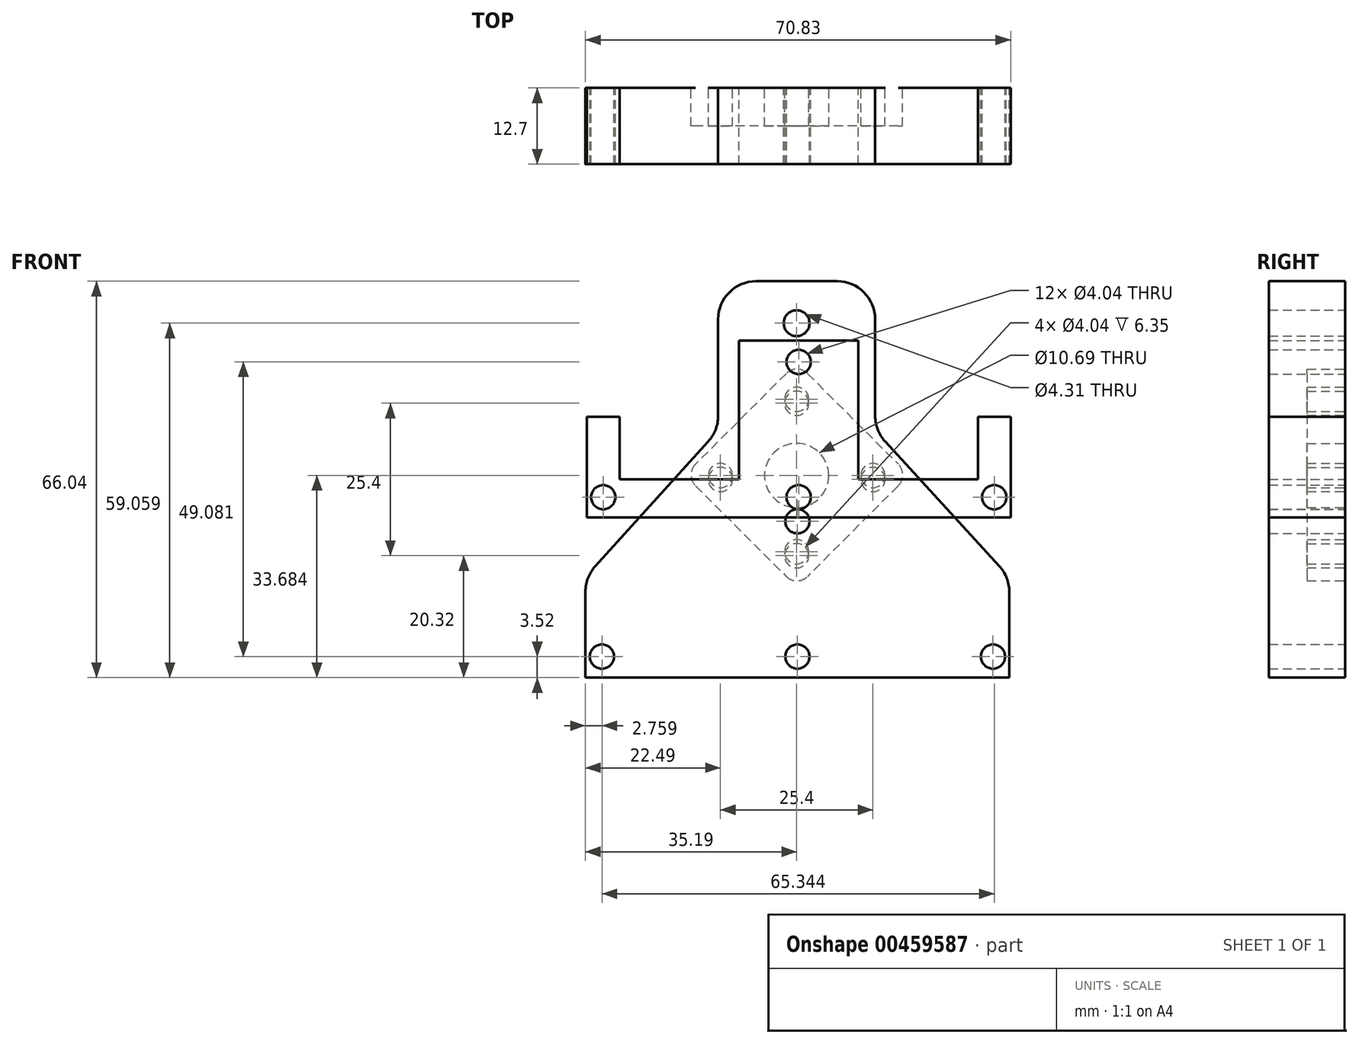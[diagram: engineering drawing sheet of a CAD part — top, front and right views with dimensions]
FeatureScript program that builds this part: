
annotation { "Feature Type Name" : "Feature", "Feature Type Description" : "" }
export const myFeature = defineFeature(function(context is Context, id is Id, definition is map)
    precondition{}
    {
        {
            var Q0;
            Q0=qCreatedBy(makeId("Front.planeOp"),FACE);
            var sketch = newSketch(context, id + "F0", { "sketchPlane" : qUnion([Q0])});
            skLineSegment(sketch, "E0.top", {"start": v(-35.19, -33.02) * mm, "end": v(34.92, -33.02) * mm});
            skLineSegment(sketch, "E1", {"start": v(35.43, -32.5) * mm, "end": v(35.43, -18.72) * mm});
            skLineSegment(sketch, "E2", {"start": v(-35.19, -33.02) * mm, "end": v(-35.19, -18.7) * mm});
            skLineSegment(sketch, "E3", {"start": v(-6.73, 33.02) * mm, "end": v(6.73, 33.02) * mm});
            skLineSegment(sketch, "E4", {"start": v(-13.08, 26.67) * mm, "end": v(-13.08, 10.58) * mm});
            skLineSegment(sketch, "E5", {"start": v(13.08, 26.67) * mm, "end": v(13.08, 10.6) * mm});
            skLineSegment(sketch, "E6", {"start": v(-14.73, 6.31) * mm, "end": v(-33.54, -14.44) * mm});
            skLineSegment(sketch, "E7", {"start": v(14.75, 6.3) * mm, "end": v(33.76, -14.43) * mm});
            skPoint(sketch, "E8.visualSharp", {"position": v(-13.08, 8.13) * mm});
            skArc(sketch, "E8.filletArc", {"start": v(-14.73, 6.31) * mm, "mid": v(-13.5, 8.3) * mm, "end": v(-13.08, 10.58) * mm});
            skPoint(sketch, "E9.visualSharp", {"position": v(13.08, 8.13) * mm});
            skArc(sketch, "E9.filletArc", {"start": v(13.08, 10.6) * mm, "mid": v(13.51, 8.3) * mm, "end": v(14.75, 6.3) * mm});
            skPoint(sketch, "E10.visualSharp", {"position": v(-13.08, 33.02) * mm});
            skArc(sketch, "E10.filletArc", {"start": v(-6.73, 33.02) * mm, "mid": v(-11.22, 31.16) * mm, "end": v(-13.08, 26.67) * mm});
            skPoint(sketch, "E11.visualSharp", {"position": v(13.08, 33.02) * mm});
            skArc(sketch, "E11.filletArc", {"start": v(13.08, 26.67) * mm, "mid": v(11.22, 31.16) * mm, "end": v(6.73, 33.02) * mm});
            skPoint(sketch, "E12.visualSharp", {"position": v(-35.19, -16.25) * mm});
            skArc(sketch, "E12.filletArc", {"start": v(-33.54, -14.44) * mm, "mid": v(-34.76, -16.42) * mm, "end": v(-35.19, -18.7) * mm});
            skPoint(sketch, "E13.visualSharp", {"position": v(35.43, -16.25) * mm});
            skArc(sketch, "E13.filletArc", {"start": v(35.43, -18.72) * mm, "mid": v(35, -16.42) * mm, "end": v(33.76, -14.43) * mm});
            skPoint(sketch, "E14.visualSharp", {"position": v(35.43, -33.02) * mm});
            skPoint(sketch, "E15.endSnap0", {"position": v(0, 33.02) * mm});
            skLineSegment(sketch, "E16", {"start": v(35.43, -32.5) * mm, "end": v(35.43, -33.02) * mm});
            skLineSegment(sketch, "E17", {"start": v(35.43, -33.02) * mm, "end": v(34.92, -33.02) * mm});
            skCircle(sketch, "E18", {"center": v(0.12, -6.97) * mm, "radius": 2.02 * mm});
            skCircle(sketch, "E19", {"center": v(32.7, -29.5) * mm, "radius": 2.02 * mm});
            skCircle(sketch, "E20", {"center": v(0.12, -29.5) * mm, "radius": 2.02 * mm});
            skCircle(sketch, "E21", {"center": v(-32.43, -29.5) * mm, "radius": 2.02 * mm});
            skLineSegment(sketch, "E22", {"start": v(-12, 19.69) * mm, "end": v(11.92, 19.69) * mm});
            skCircle(sketch, "E23", {"center": v(0, 26.04) * mm, "radius": 2.15 * mm});
            skSolve(sketch);
        }
        {
            var Q0;
            Q0=makeQuery(id+"F0.imprint","IMPRINT",FACE,{"disambiguationData":[TD([[makeQuery(id+"F0.imprint","IMPRINT",EDGE,{"derivedFrom":sQuery(id+"F0.wireOp",EDGE,"E0.top")}),1.0]])]});
            extrude(context, id + "F1", {"entities" : qUnion([Q0]), "depth" : 12.7 * mm});
        }
        {
            var Q0;
            Q0=makeQuery(id+"F1.opExtrude","CAP_FACE",FACE,{"disambiguationData":[OSD([sQuery(id+"F0.wireOp",EDGE,"E0.top"),sQuery(id+"F0.wireOp",EDGE,"E1"),sQuery(id+"F0.wireOp",EDGE,"E2"),sQuery(id+"F0.wireOp",EDGE,"E3"),sQuery(id+"F0.wireOp",EDGE,"E4"),sQuery(id+"F0.wireOp",EDGE,"E5"),sQuery(id+"F0.wireOp",EDGE,"E6"),sQuery(id+"F0.wireOp",EDGE,"E7"),sQuery(id+"F0.wireOp",EDGE,"E8.filletArc"),sQuery(id+"F0.wireOp",EDGE,"E9.filletArc"),sQuery(id+"F0.wireOp",EDGE,"E10.filletArc"),sQuery(id+"F0.wireOp",EDGE,"E11.filletArc"),sQuery(id+"F0.wireOp",EDGE,"E12.filletArc"),sQuery(id+"F0.wireOp",EDGE,"E13.filletArc"),sQuery(id+"F0.wireOp",EDGE,"E14.filletArc")])],"isStart":true});
            var sketch = newSketch(context, id + "F2", { "sketchPlane" : qUnion([Q0])});
            skCircle(sketch, "E24", {"center": v(0, 12.7) * mm, "radius": 2.02 * mm});
            skCircle(sketch, "E25", {"center": v(12.7, 0) * mm, "radius": 2.02 * mm});
            skCircle(sketch, "E26", {"center": v(0, -12.7) * mm, "radius": 2.02 * mm});
            skCircle(sketch, "E27", {"center": v(-12.7, 0) * mm, "radius": 2.02 * mm});
            skSolve(sketch);
        }
        {
            var Q0;
            Q0=makeQuery(id+"F2.imprint","IMPRINT",FACE,{"disambiguationData":[TD([[makeQuery(id+"F2.imprint","IMPRINT",EDGE,{"derivedFrom":sQuery(id+"F2.wireOp",EDGE,"E24")}),1.0]])]});
            var Q1;
            Q1=makeQuery(id+"F2.imprint","IMPRINT",FACE,{"disambiguationData":[TD([[makeQuery(id+"F2.imprint","IMPRINT",EDGE,{"derivedFrom":sQuery(id+"F2.wireOp",EDGE,"E27")}),1.0]])]});
            var Q2;
            Q2=makeQuery(id+"F2.imprint","IMPRINT",FACE,{"disambiguationData":[TD([[makeQuery(id+"F2.imprint","IMPRINT",EDGE,{"derivedFrom":sQuery(id+"F2.wireOp",EDGE,"E25")}),1.0]])]});
            var Q3;
            Q3=makeQuery(id+"F2.imprint","IMPRINT",FACE,{"disambiguationData":[TD([[makeQuery(id+"F2.imprint","IMPRINT",EDGE,{"derivedFrom":sQuery(id+"F2.wireOp",EDGE,"E26")}),1.0]])]});
            extrude(context, id + "F3", {"entities" : qUnion([Q0, Q1, Q2, Q3]), "operationType" : NewBodyOperationType.REMOVE, "oppositeDirection" : true, "depth" : 6.35 * mm});
        }
        {
            var Q0;
            Q0=makeQuery(id+"F1.opExtrude","CAP_FACE",FACE,{"disambiguationData":[OSD([sQuery(id+"F0.wireOp",EDGE,"E0.top"),sQuery(id+"F0.wireOp",EDGE,"E1"),sQuery(id+"F0.wireOp",EDGE,"E2"),sQuery(id+"F0.wireOp",EDGE,"E3"),sQuery(id+"F0.wireOp",EDGE,"E4"),sQuery(id+"F0.wireOp",EDGE,"E5"),sQuery(id+"F0.wireOp",EDGE,"E6"),sQuery(id+"F0.wireOp",EDGE,"E7"),sQuery(id+"F0.wireOp",EDGE,"E8.filletArc"),sQuery(id+"F0.wireOp",EDGE,"E9.filletArc"),sQuery(id+"F0.wireOp",EDGE,"E10.filletArc"),sQuery(id+"F0.wireOp",EDGE,"E11.filletArc"),sQuery(id+"F0.wireOp",EDGE,"E12.filletArc"),sQuery(id+"F0.wireOp",EDGE,"E13.filletArc"),sQuery(id+"F0.wireOp",EDGE,"E14.filletArc")])],"isStart":true});
            var sketch = newSketch(context, id + "F4", { "sketchPlane" : qUnion([Q0])});
            skLineSegment(sketch, "E28.bottom", {"start": v(-1.8, 16.88) * mm, "end": v(-16.88, 1.8) * mm});
            skLineSegment(sketch, "E28.top", {"start": v(16.88, -1.8) * mm, "end": v(1.8, -16.88) * mm});
            skLineSegment(sketch, "E28.left", {"start": v(1.8, 16.88) * mm, "end": v(16.88, 1.8) * mm});
            skLineSegment(sketch, "E28.right", {"start": v(-16.88, -1.8) * mm, "end": v(-1.8, -16.88) * mm});
            skPoint(sketch, "E28.middle", {"position": v(0, 0) * mm});
            skPoint(sketch, "E29.visualSharp", {"position": v(0, 18.68) * mm});
            skArc(sketch, "E29.filletArc", {"start": v(1.8, 16.88) * mm, "mid": v(0, 17.63) * mm, "end": v(-1.8, 16.88) * mm});
            skPoint(sketch, "E30.visualSharp", {"position": v(-18.68, 0) * mm});
            skArc(sketch, "E30.filletArc", {"start": v(-16.88, 1.8) * mm, "mid": v(-17.63, 0) * mm, "end": v(-16.88, -1.8) * mm});
            skPoint(sketch, "E31.visualSharp", {"position": v(0, -18.68) * mm});
            skArc(sketch, "E31.filletArc", {"start": v(-1.8, -16.88) * mm, "mid": v(0, -17.63) * mm, "end": v(1.8, -16.88) * mm});
            skPoint(sketch, "E32.visualSharp", {"position": v(18.68, 0) * mm});
            skArc(sketch, "E32.filletArc", {"start": v(16.88, -1.8) * mm, "mid": v(17.63, 0) * mm, "end": v(16.88, 1.8) * mm});
            skSolve(sketch);
        }
        {
            var Q0;
            Q0=makeQuery(id+"F4.imprint","IMPRINT",FACE,{"disambiguationData":[TD([[makeQuery(id+"F4.imprint","IMPRINT",EDGE,{"derivedFrom":sQuery(id+"F4.wireOp",EDGE,"E28.bottom")}),1.0]])]});
            extrude(context, id + "F5", {"entities" : qUnion([Q0]), "depth" : 6.35 * mm});
        }
        {
            var Q0;
            Q0=qCreatedBy(makeId("Front.planeOp"),FACE);
            var sketch = newSketch(context, id + "F6", { "sketchPlane" : qUnion([Q0])});
            skLineSegment(sketch, "E33", {"start": v(35.64, -6.35) * mm, "end": v(-34.97, -6.35) * mm});
            skLineSegment(sketch, "E34", {"start": v(35.64, -6.35) * mm, "end": v(35.64, 10.41) * mm});
            skLineSegment(sketch, "E35", {"start": v(-34.97, -6.35) * mm, "end": v(-34.97, 10.41) * mm});
            skLineSegment(sketch, "E36", {"start": v(35.64, 10.41) * mm, "end": v(30.18, 10.41) * mm});
            skLineSegment(sketch, "E37", {"start": v(-34.97, 10.41) * mm, "end": v(-29.5, 10.41) * mm});
            skLineSegment(sketch, "E38", {"start": v(30.18, 0) * mm, "end": v(10.3, 0) * mm});
            skLineSegment(sketch, "E39", {"start": v(-9.62, 23.11) * mm, "end": v(10.3, 23.11) * mm});
            skLineSegment(sketch, "E40", {"start": v(30.18, 10.41) * mm, "end": v(30.18, 0) * mm});
            skLineSegment(sketch, "E41", {"start": v(10.3, 23.11) * mm, "end": v(10.3, 0) * mm});
            skLineSegment(sketch, "E42", {"start": v(-9.62, 23.11) * mm, "end": v(-9.62, 0) * mm});
            skLineSegment(sketch, "E43", {"start": v(-29.5, 10.41) * mm, "end": v(-29.5, 0) * mm});
            skLineSegment(sketch, "E44", {"start": v(-29.5, 0) * mm, "end": v(-9.62, 0) * mm});
            skCircle(sketch, "E45", {"center": v(0.34, 19.58) * mm, "radius": 2.02 * mm});
            skCircle(sketch, "E46", {"center": v(32.91, -2.95) * mm, "radius": 2.02 * mm});
            skCircle(sketch, "E47", {"center": v(0.34, -2.95) * mm, "radius": 2.02 * mm});
            skCircle(sketch, "E48", {"center": v(-32.22, -2.95) * mm, "radius": 2.02 * mm});
            skPoint(sketch, "E49", {"position": v(4.04, 9.76) * mm});
            skSolve(sketch);
        }
        {
            var Q0;
            Q0=makeQuery(id+"F6.imprint","IMPRINT",FACE,{"disambiguationData":[TD([[makeQuery(id+"F6.imprint","IMPRINT",EDGE,{"derivedFrom":sQuery(id+"F6.wireOp",EDGE,"E33")}),-1.0]])]});
            extrude(context, id + "F7", {"entities" : qUnion([Q0]), "depth" : 12.7 * mm});
        }
        {
            var Q0;
            Q0=qCreatedBy(makeId("Front.planeOp"),FACE);
            var sketch = newSketch(context, id + "F8", { "sketchPlane" : qUnion([Q0])});
            skCircle(sketch, "E50", {"center": v(0, 13.36) * mm, "radius": 2.02 * mm});
            skCircle(sketch, "E51", {"center": v(12.7, 0.66) * mm, "radius": 2.02 * mm});
            skCircle(sketch, "E52", {"center": v(0, -12.04) * mm, "radius": 2.02 * mm});
            skCircle(sketch, "E53", {"center": v(-12.7, 0.66) * mm, "radius": 2.02 * mm});
            skLineSegment(sketch, "E54.bottom", {"start": v(-1.76, 17.63) * mm, "end": v(-16.84, 2.54) * mm});
            skLineSegment(sketch, "E54.top", {"start": v(16.92, -1.05) * mm, "end": v(1.84, -16.14) * mm});
            skLineSegment(sketch, "E54.left", {"start": v(1.84, 17.63) * mm, "end": v(16.92, 2.54) * mm});
            skLineSegment(sketch, "E54.right", {"start": v(-16.84, -1.05) * mm, "end": v(-1.76, -16.14) * mm});
            skArc(sketch, "E55.filletArc", {"start": v(1.84, 17.63) * mm, "mid": v(0.04, 18.37) * mm, "end": v(-1.76, 17.63) * mm});
            skArc(sketch, "E56.filletArc", {"start": v(-16.84, 2.54) * mm, "mid": v(-17.59, 0.75) * mm, "end": v(-16.84, -1.05) * mm});
            skArc(sketch, "E57.filletArc", {"start": v(-1.76, -16.14) * mm, "mid": v(0.04, -16.88) * mm, "end": v(1.84, -16.14) * mm});
            skArc(sketch, "E58.filletArc", {"start": v(16.92, -1.05) * mm, "mid": v(17.67, 0.75) * mm, "end": v(16.92, 2.54) * mm});
            skCircle(sketch, "E59", {"center": v(0, 0.66) * mm, "radius": 5.35 * mm});
            skSolve(sketch);
        }
        {
            var Q0;
            Q0=makeQuery(id+"F8.imprint","IMPRINT",FACE,{"disambiguationData":[TD([[makeQuery(id+"F8.imprint","IMPRINT",EDGE,{"derivedFrom":sQuery(id+"F8.wireOp",EDGE,"E50")}),-1.0]])]});
            extrude(context, id + "F9", {"entities" : qUnion([Q0]), "depth" : 6.35 * mm});
        }
        {
            var Q0;
            Q0=makeQuery(id+"F5.opExtrude","SWEPT_BODY",BODY,{"disambiguationData":[OSD([sQuery(id+"F0.wireOp",EDGE,"E18"),sQuery(id+"F2.wireOp",EDGE,"E24"),sQuery(id+"F2.wireOp",EDGE,"E25"),sQuery(id+"F2.wireOp",EDGE,"E26"),sQuery(id+"F2.wireOp",EDGE,"E27"),sQuery(id+"F4.wireOp",EDGE,"E28.bottom"),sQuery(id+"F4.wireOp",EDGE,"E28.top"),sQuery(id+"F4.wireOp",EDGE,"E28.left"),sQuery(id+"F4.wireOp",EDGE,"E28.right"),sQuery(id+"F4.wireOp",EDGE,"E29.filletArc"),sQuery(id+"F4.wireOp",EDGE,"E30.filletArc"),sQuery(id+"F4.wireOp",EDGE,"E31.filletArc"),sQuery(id+"F4.wireOp",EDGE,"E32.filletArc")])]});
            deleteBodies(context, id + "F10", {"entities" : qUnion([Q0])});
        }
    });
